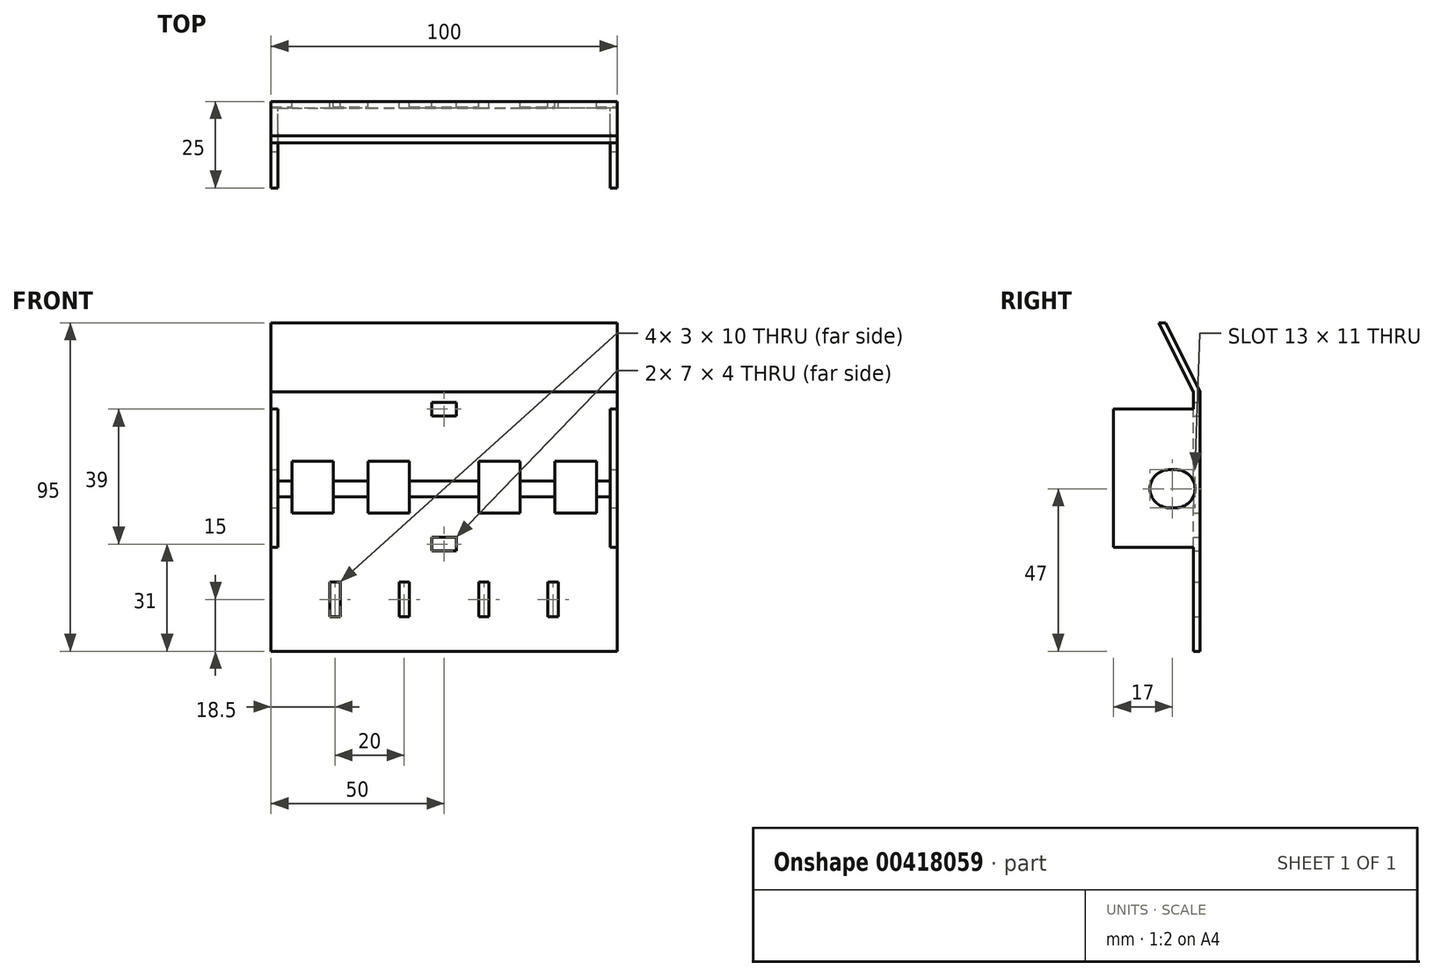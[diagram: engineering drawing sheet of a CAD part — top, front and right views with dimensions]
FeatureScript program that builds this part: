
annotation { "Feature Type Name" : "Feature", "Feature Type Description" : "" }
export const myFeature = defineFeature(function(context is Context, id is Id, definition is map)
    precondition{}
    {
        {
            var Q0;
            Q0=qCreatedBy(makeId("Front.planeOp"),FACE);
            var sketch = newSketch(context, id + "F0", { "sketchPlane" : qUnion([Q0])});
            skLineSegment(sketch, "E0", {"start": v(-44, 23) * mm, "end": v(-44, 8) * mm});
            skLineSegment(sketch, "E1", {"start": v(22, 23) * mm, "end": v(22, 8) * mm});
            skLineSegment(sketch, "E2", {"start": v(-32, 23) * mm, "end": v(-32, 8) * mm});
            skLineSegment(sketch, "E3", {"start": v(-22, 23) * mm, "end": v(-22, 8) * mm});
            skLineSegment(sketch, "E4", {"start": v(-10, 23) * mm, "end": v(-10, 8) * mm});
            skLineSegment(sketch, "E5", {"start": v(10, 23) * mm, "end": v(10, 8) * mm});
            skPoint(sketch, "E6.orphan", {"position": v(10, -2.09) * mm});
            skPoint(sketch, "E7.orphan", {"position": v(-10, -2.09) * mm});
            skPoint(sketch, "E8.orphan", {"position": v(-22, -2.09) * mm});
            skPoint(sketch, "E9.orphan", {"position": v(-32, -2.09) * mm});
            skLineSegment(sketch, "E10.bottom", {"start": v(-44, 23) * mm, "end": v(-32, 23) * mm});
            skLineSegment(sketch, "E10.top", {"start": v(-44, 8) * mm, "end": v(-32, 8) * mm});
            skPoint(sketch, "E11.start.orphan", {"position": v(53.75, -5.74) * mm});
            skPoint(sketch, "E12.left.start.orphan", {"position": v(40.08, -5.74) * mm});
            skLineSegment(sketch, "E13.trimOffspring", {"start": v(-22, 23) * mm, "end": v(-10, 23) * mm});
            skLineSegment(sketch, "E14.trimOffspring", {"start": v(-22, 8) * mm, "end": v(-10, 8) * mm});
            skLineSegment(sketch, "E15.trimOffspring", {"start": v(10, 8) * mm, "end": v(22, 8) * mm});
            skLineSegment(sketch, "E16.trimOffspring", {"start": v(10, 23) * mm, "end": v(22, 23) * mm});
            skLineSegment(sketch, "E17.bottom", {"start": v(-50, 43) * mm, "end": v(50, 43) * mm});
            skLineSegment(sketch, "E17.top", {"start": v(-50, -7) * mm, "end": v(50, -7) * mm, "construction": true});
            skLineSegment(sketch, "E17.left", {"start": v(-50, 43) * mm, "end": v(-50, -32) * mm});
            skLineSegment(sketch, "E17.right", {"start": v(50, 43) * mm, "end": v(50, -32) * mm});
            skLineSegment(sketch, "E18.bottom", {"start": v(3.5, -3) * mm, "end": v(-3.5, -3) * mm});
            skLineSegment(sketch, "E18.top", {"start": v(3.5, 1) * mm, "end": v(-3.5, 1) * mm});
            skLineSegment(sketch, "E18.left", {"start": v(3.5, -3) * mm, "end": v(3.5, 1) * mm});
            skLineSegment(sketch, "E18.right", {"start": v(-3.5, -3) * mm, "end": v(-3.5, 1) * mm});
            skLineSegment(sketch, "E19.bottom", {"start": v(3.5, 36) * mm, "end": v(-3.5, 36) * mm});
            skLineSegment(sketch, "E19.top", {"start": v(3.5, 40) * mm, "end": v(-3.5, 40) * mm});
            skLineSegment(sketch, "E19.left", {"start": v(3.5, 36) * mm, "end": v(3.5, 40) * mm});
            skLineSegment(sketch, "E19.right", {"start": v(-3.5, 36) * mm, "end": v(-3.5, 40) * mm});
            skLineSegment(sketch, "E20", {"start": v(50, -32) * mm, "end": v(-50, -32) * mm});
            skLineSegment(sketch, "E21.bottom", {"start": v(33, -22) * mm, "end": v(30, -22) * mm});
            skLineSegment(sketch, "E21.top", {"start": v(33, -12) * mm, "end": v(30, -12) * mm});
            skLineSegment(sketch, "E21.left", {"start": v(33, -22) * mm, "end": v(33, -12) * mm});
            skLineSegment(sketch, "E21.right", {"start": v(30, -22) * mm, "end": v(30, -12) * mm});
            skLineSegment(sketch, "E22.bottom", {"start": v(13, -22) * mm, "end": v(10, -22) * mm});
            skLineSegment(sketch, "E22.top", {"start": v(13, -12) * mm, "end": v(10, -12) * mm});
            skLineSegment(sketch, "E22.left", {"start": v(13, -22) * mm, "end": v(13, -12) * mm});
            skLineSegment(sketch, "E22.right", {"start": v(10, -22) * mm, "end": v(10, -12) * mm});
            skPoint(sketch, "E23.right.end.orphan", {"position": v(0, -24.35) * mm});
            skLineSegment(sketch, "E24.bottom", {"start": v(-30, -22) * mm, "end": v(-33, -22) * mm});
            skLineSegment(sketch, "E24.top", {"start": v(-30, -12) * mm, "end": v(-33, -12) * mm});
            skLineSegment(sketch, "E24.left", {"start": v(-30, -22) * mm, "end": v(-30, -12) * mm});
            skLineSegment(sketch, "E24.right", {"start": v(-33, -22) * mm, "end": v(-33, -12) * mm});
            skLineSegment(sketch, "E25.bottom", {"start": v(-10, -22) * mm, "end": v(-13, -22) * mm});
            skLineSegment(sketch, "E25.top", {"start": v(-10, -12) * mm, "end": v(-13, -12) * mm});
            skLineSegment(sketch, "E25.left", {"start": v(-10, -22) * mm, "end": v(-10, -12) * mm});
            skLineSegment(sketch, "E25.right", {"start": v(-13, -22) * mm, "end": v(-13, -12) * mm});
            skPoint(sketch, "E26.orphan", {"position": v(52.85, -18.82) * mm});
            skPoint(sketch, "E27.orphan", {"position": v(-50, -32) * mm});
            skPoint(sketch, "E28.end.orphan", {"position": v(47, -18.82) * mm});
            skPoint(sketch, "E29.orphan", {"position": v(-50, -18.82) * mm});
            skLineSegment(sketch, "E30.bottom", {"start": v(44, 23) * mm, "end": v(32, 23) * mm});
            skLineSegment(sketch, "E30.top", {"start": v(44, 8) * mm, "end": v(32, 8) * mm});
            skLineSegment(sketch, "E30.left", {"start": v(44, 23) * mm, "end": v(44, 8) * mm});
            skLineSegment(sketch, "E30.right", {"start": v(32, 23) * mm, "end": v(32, 8) * mm});
            skSolve(sketch);
        }
        {
            var Q0;
            Q0 = qSketchRegion(id + "F0", true);
            extrude(context, id + "F1", {"entities" : qUnion([Q0]), "depth" : 2 * mm, "offsetDistance" : 25 * mm});
        }
        {
            var Q0;
            Q0=makeQuery(id+"F1.opExtrude","CAP_FACE",FACE,{"disambiguationData":[OSD([sQuery(id+"F0.wireOp",EDGE,"E0"),sQuery(id+"F0.wireOp",EDGE,"E1"),sQuery(id+"F0.wireOp",EDGE,"E2"),sQuery(id+"F0.wireOp",EDGE,"E3"),sQuery(id+"F0.wireOp",EDGE,"E4"),sQuery(id+"F0.wireOp",EDGE,"E5"),sQuery(id+"F0.wireOp",EDGE,"E10.bottom"),sQuery(id+"F0.wireOp",EDGE,"E10.top"),sQuery(id+"F0.wireOp",EDGE,"E13.trimOffspring"),sQuery(id+"F0.wireOp",EDGE,"E14.trimOffspring"),sQuery(id+"F0.wireOp",EDGE,"E15.trimOffspring"),sQuery(id+"F0.wireOp",EDGE,"E16.trimOffspring"),sQuery(id+"F0.wireOp",EDGE,"E17.bottom"),sQuery(id+"F0.wireOp",EDGE,"E17.top"),sQuery(id+"F0.wireOp",EDGE,"E17.left"),sQuery(id+"F0.wireOp",EDGE,"E17.right")])],"isStart":true});
            var sketch = newSketch(context, id + "F2", { "sketchPlane" : qUnion([Q0])});
            skLineSegment(sketch, "E31.bottom", {"start": v(-48, 38) * mm, "end": v(-50, 38) * mm});
            skLineSegment(sketch, "E31.top", {"start": v(-48, -2) * mm, "end": v(-50, -2) * mm});
            skLineSegment(sketch, "E31.left", {"start": v(-48, 38) * mm, "end": v(-48, -2) * mm});
            skLineSegment(sketch, "E31.right", {"start": v(-50, 38) * mm, "end": v(-50, -2) * mm});
            skLineSegment(sketch, "E32.bottom", {"start": v(50, 38) * mm, "end": v(48, 38) * mm});
            skLineSegment(sketch, "E32.top", {"start": v(50, -2) * mm, "end": v(48, -2) * mm});
            skLineSegment(sketch, "E32.left", {"start": v(50, 38) * mm, "end": v(50, -2) * mm});
            skLineSegment(sketch, "E32.right", {"start": v(48, 38) * mm, "end": v(48, -2) * mm});
            skSolve(sketch);
        }
        {
            var Q0;
            Q0 = qSketchRegion(id + "F2", true);
            extrude(context, id + "F3", {"entities" : qUnion([Q0]), "operationType" : NewBodyOperationType.ADD, "oppositeDirection" : true, "depth" : 25 * mm, "offsetDistance" : 25 * mm});
        }
        {
            var Q0;
            Q0=makeQuery(id+"F1.opExtrude","SWEPT_FACE",FACE,{"disambiguationData":[OSD([sQuery(id+"F0.wireOp",EDGE,"E17.left")])]});
            var sketch = newSketch(context, id + "F4", { "sketchPlane" : qUnion([Q0])});
            skLineSegment(sketch, "E33", {"start": v(2, 43) * mm, "end": v(0, 43) * mm});
            skLineSegment(sketch, "E34", {"start": v(0, 43) * mm, "end": v(10, 63) * mm});
            skLineSegment(sketch, "E35", {"start": v(10, 63) * mm, "end": v(12, 63) * mm});
            skLineSegment(sketch, "E36", {"start": v(12, 63) * mm, "end": v(2, 43) * mm});
            skSolve(sketch);
        }
        {
            var Q0;
            Q0 = qSketchRegion(id + "F4", true);
            extrude(context, id + "F5", {"entities" : qUnion([Q0]), "operationType" : NewBodyOperationType.ADD, "oppositeDirection" : true, "depth" : 100 * mm, "offsetDistance" : 25 * mm});
        }
        {
            var Q0;
            Q0=makeQuery(id+"F3.opExtrude","SWEPT_FACE",FACE,{"disambiguationData":[OSD([sQuery(id+"F2.wireOp",EDGE,"E31.right")])]});
            var sketch = newSketch(context, id + "F6", { "sketchPlane" : qUnion([Q0])});
            skArc(sketch, "E37", {"start": v(-9, 20.5) * mm, "mid": v(-14.5, 15) * mm, "end": v(-9, 9.5) * mm});
            skLineSegment(sketch, "E38", {"start": v(-9, 15) * mm, "end": v(15.2, 15) * mm, "construction": true});
            skLineSegment(sketch, "E39", {"start": v(-9, 20.5) * mm, "end": v(-9, 23.77) * mm, "construction": true});
            skLineSegment(sketch, "E40", {"start": v(-7, 20.5) * mm, "end": v(-7, 30.1) * mm, "construction": true});
            skLineSegment(sketch, "E41", {"start": v(-9, 9.5) * mm, "end": v(-9, 5.35) * mm, "construction": true});
            skLineSegment(sketch, "E42", {"start": v(-7, 9.5) * mm, "end": v(-7, 6.7) * mm, "construction": true});
            skLineSegment(sketch, "E43", {"start": v(-9, 9.5) * mm, "end": v(-7, 9.5) * mm});
            skLineSegment(sketch, "E44", {"start": v(-7, 20.5) * mm, "end": v(-9, 20.5) * mm});
            skArc(sketch, "E45.trimOffspring", {"start": v(-7, 9.5) * mm, "mid": v(-1.5, 15) * mm, "end": v(-7, 20.5) * mm});
            skSolve(sketch);
        }
        {
            var Q0;
            Q0 = qSketchRegion(id + "F6", true);
            extrude(context, id + "F7", {"entities" : qUnion([Q0]), "operationType" : NewBodyOperationType.REMOVE, "oppositeDirection" : true, "depth" : 100 * mm, "offsetDistance" : 25 * mm});
        }
    });
